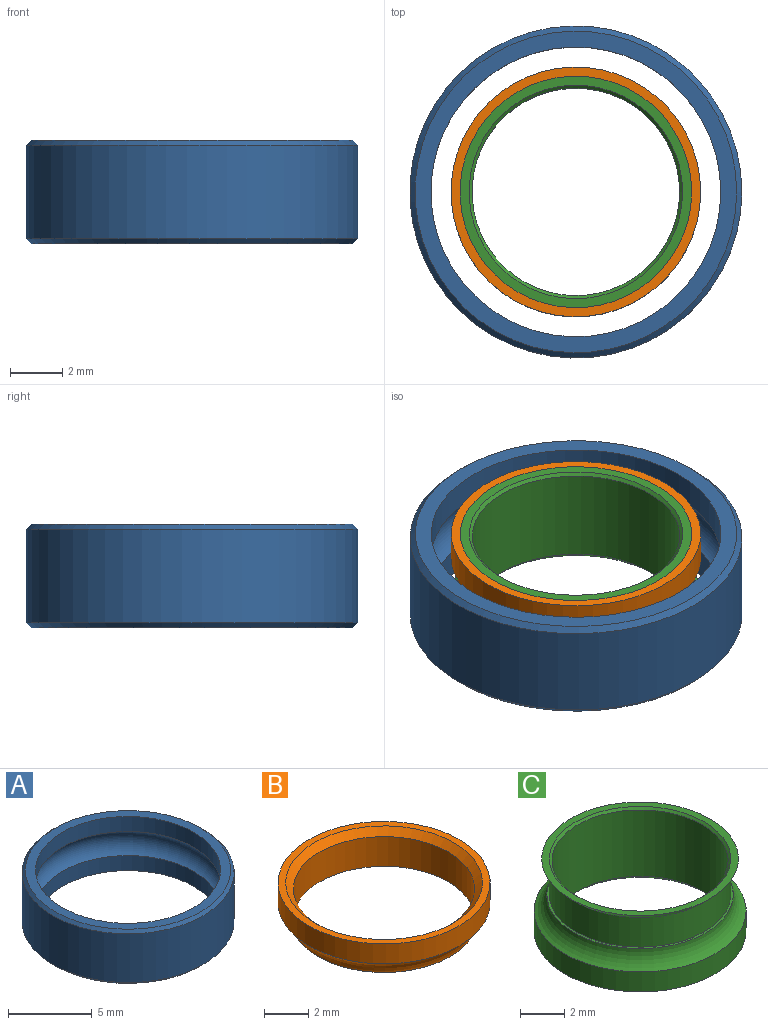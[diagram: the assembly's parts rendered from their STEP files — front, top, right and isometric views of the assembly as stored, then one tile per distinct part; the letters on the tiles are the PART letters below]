
ASSEMBLY  parts=3 mates=4
PART A: 8 faces, bbox 13.3x13.3x4 mm
  f0: cylinder r=5.54mm len=11.09mm, axis (0,0,1), area 38.4mm2, adj f1,f7
  f1: torus R=5.16mm, axis (0,0,1), area 83mm2, adj f0,f2
  f2: cylinder r=5.54mm len=11.09mm, axis (0,0,1), area 38.4mm2, adj f1,f6
  f3: cone r=6.15mm half-angle=45deg, axis (0,0,1), area 11mm2, adj f4,f6
  f4: cylinder r=6.35mm len=12.7mm, axis (0,0,1), area 142.5mm2, adj f3,f5
  f5: cone r=6.35mm half-angle=45deg, axis (0,0,-1), area 11mm2, adj f4,f7
  f6: plane 12.3x12.3mm, normal (0,0,-1), area 22.4mm2, adj f2,f3
  f7: plane 12.3x12.3mm, normal (0,0,1), area 22.4mm2, adj f0,f5
PART B: 6 faces, bbox 11.2x11.2x2.7 mm
  f0: cylinder r=4.78mm len=9.55mm, axis (0,0,1), area 33.1mm2, adj f1,f4
  f1: torus R=5.16mm, axis (0,0,1), area 30.8mm2, adj f0,f5
  f2: cylinder r=4.08mm len=8.17mm, axis (0,0,1), area 42mm2, adj f3,f5
  f3: cone r=4.43mm half-angle=45deg, axis (0,0,1), area 13.1mm2, adj f2,f4
  f4: plane 9.55x9.55mm, normal (0,0,1), area 10mm2, adj f0,f3
  f5: plane 8.4x8.4mm, normal (0,0,-1), area 3mm2, adj f1,f2
PART C: 10 faces, bbox 11.2x11.2x4 mm
  f0: cone r=4.08mm half-angle=45deg, axis (0,0,1), area 4.1mm2, adj f1,f7
  f1: cylinder r=3.97mm len=7.94mm, axis (0,0,1), area 91.2mm2, adj f0,f2
  f2: cone r=3.97mm half-angle=45deg, axis (0,0,-1), area 7.2mm2, adj f1,f9
  f3: cylinder r=4.78mm len=9.55mm, axis (0,0,1), area 33.1mm2, adj f4,f9
  f4: torus R=5.16mm, axis (0,0,1), area 30.8mm2, adj f3,f8
  f5: cylinder r=4.08mm len=8.17mm, axis (0,0,1), area 42mm2, adj f6,f8
  f6: cone r=4.08mm half-angle=45deg, axis (0,0,1), area 13.1mm2, adj f5,f7
  f7: plane 8.86x8.86mm, normal (0,0,1), area 9.3mm2, adj f0,f6
  f8: plane 8.4x8.4mm, normal (0,0,1), area 3mm2, adj f4,f5
  f9: plane 9.55x9.55mm, normal (0,0,-1), area 17.1mm2, adj f2,f3
PLACE A t=(-0.91,1.77,-1.3)mm
PLACE B t=(-0.91,1.77,-1.3)mm
PLACE C t=(-0.91,1.77,-1.3)mm
MATE cylindrical B.f0 <-> C.f0  axis (0,0,1) through (-0.91,1.77,-1.3)mm
MATE planar B.f0 <-> A.f0  axis (0,0,1) through (-0.91,1.77,0.68)mm
MATE planar C.f0 <-> B.f0  axis (0,0,1) through (-0.91,1.77,-1.3)mm
MATE cylindrical C.f0 <-> A.f0  axis (0,0,1) through (-0.91,1.77,-3.29)mm
